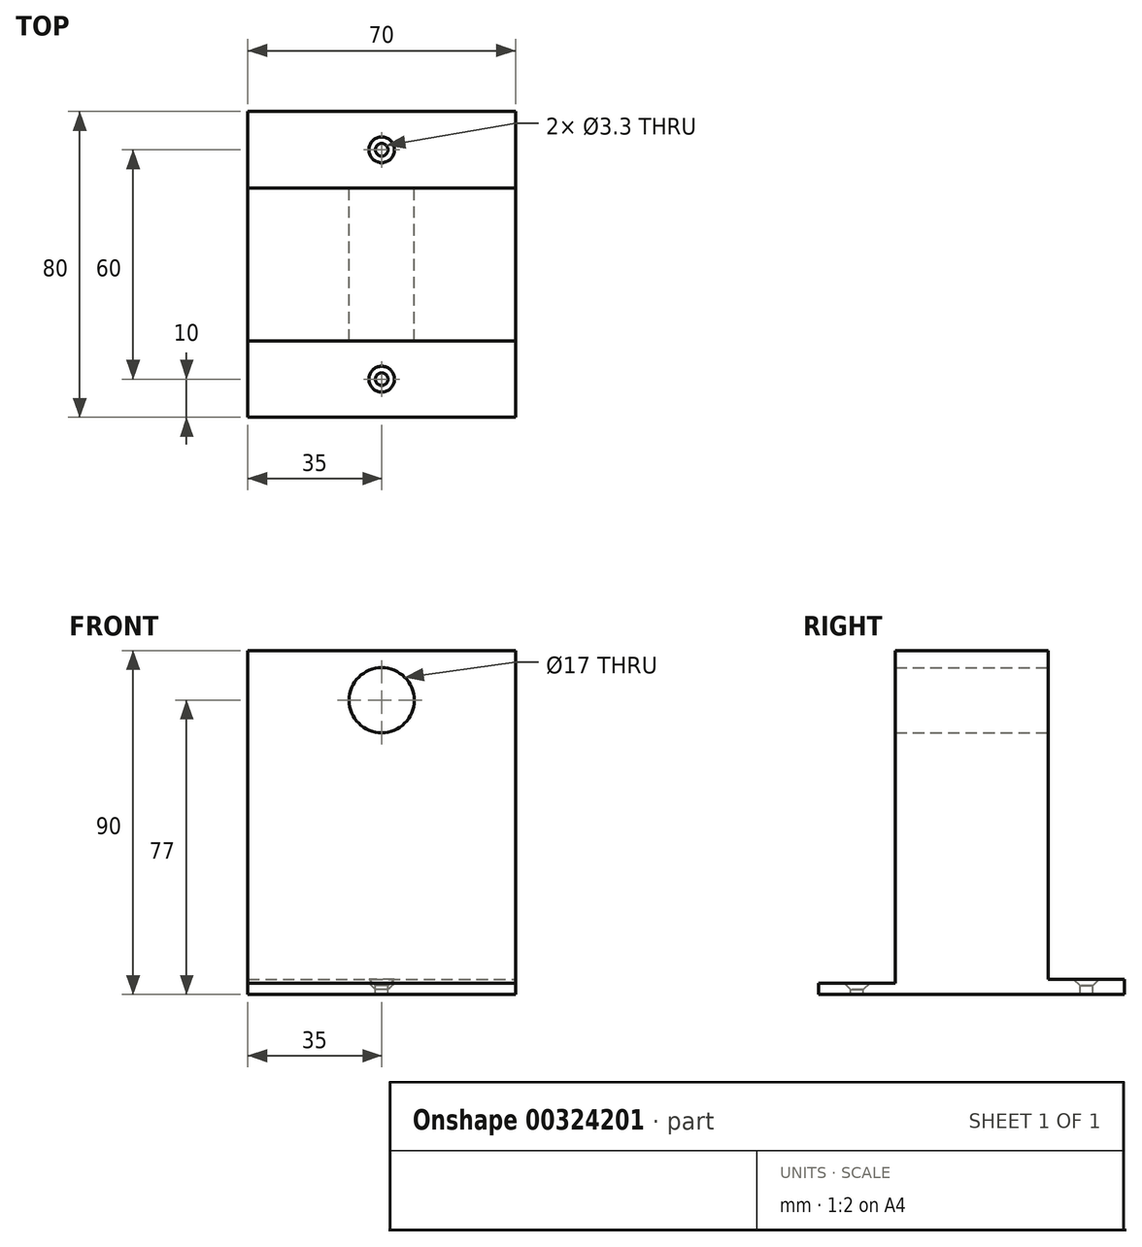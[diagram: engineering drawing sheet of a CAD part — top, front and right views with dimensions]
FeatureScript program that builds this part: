
annotation { "Feature Type Name" : "Feature", "Feature Type Description" : "" }
export const myFeature = defineFeature(function(context is Context, id is Id, definition is map)
    precondition{}
    {
        {
            var Q0;
            Q0=qCreatedBy(makeId("Top.planeOp"),FACE);
            var sketch = newSketch(context, id + "F0", { "sketchPlane" : qUnion([Q0])});
            skLineSegment(sketch, "E0.bottom", {"start": v(-35, 20) * mm, "end": v(35, 20) * mm});
            skLineSegment(sketch, "E0.top", {"start": v(-35, -20) * mm, "end": v(35, -20) * mm});
            skLineSegment(sketch, "E0.left", {"start": v(-35, 20) * mm, "end": v(-35, -20) * mm});
            skLineSegment(sketch, "E0.right", {"start": v(35, 20) * mm, "end": v(35, -20) * mm});
            skSolve(sketch);
        }
        {
            var Q0;
            Q0 = qSketchRegion(id + "F0", true);
            extrude(context, id + "F1", {"entities" : qUnion([Q0]), "depth" : 90 * mm});
        }
        {
            var Q0;
            Q0=makeQuery(id+"F1.opExtrude","SWEPT_FACE",FACE,{"disambiguationData":[OSD([sQuery(id+"F0.wireOp",EDGE,"E0.bottom")])]});
            var sketch = newSketch(context, id + "F2", { "sketchPlane" : qUnion([Q0])});
            skCircle(sketch, "E1", {"center": v(0, 77) * mm, "radius": 8.5 * mm});
            skLineSegment(sketch, "E2", {"start": v(0, 77) * mm, "end": v(0, 0) * mm});
            skSolve(sketch);
        }
        {
            var Q0;
            Q0 = qSketchRegion(id + "F2", true);
            extrude(context, id + "F3", {"entities" : qUnion([Q0]), "operationType" : NewBodyOperationType.REMOVE, "endBound" : BoundingType.THROUGH_ALL, "oppositeDirection" : true, "depth" : 25 * mm});
        }
        {
            var Q0;
            Q0=makeQuery(id+"F1.opExtrude","SWEPT_FACE",FACE,{"disambiguationData":[OSD([sQuery(id+"F0.wireOp",EDGE,"E0.top")])]});
            var sketch = newSketch(context, id + "F4", { "sketchPlane" : qUnion([Q0])});
            skLineSegment(sketch, "E3.bottom", {"start": v(-35, 3) * mm, "end": v(35, 3) * mm});
            skLineSegment(sketch, "E3.top", {"start": v(-35, 0) * mm, "end": v(35, 0) * mm});
            skLineSegment(sketch, "E3.left", {"start": v(-35, 3) * mm, "end": v(-35, 0) * mm});
            skLineSegment(sketch, "E3.right", {"start": v(35, 3) * mm, "end": v(35, 0) * mm});
            skSolve(sketch);
        }
        {
            var Q0;
            Q0 = qSketchRegion(id + "F4", true);
            extrude(context, id + "F5", {"entities" : qUnion([Q0]), "operationType" : NewBodyOperationType.ADD, "depth" : 20 * mm});
        }
        {
            var Q0;
            Q0=makeQuery(id+"F1.opExtrude","SWEPT_FACE",FACE,{"disambiguationData":[OSD([sQuery(id+"F0.wireOp",EDGE,"E0.bottom")])]});
            var sketch = newSketch(context, id + "F6", { "sketchPlane" : qUnion([Q0])});
            skLineSegment(sketch, "E4.bottom", {"start": v(35, 0) * mm, "end": v(-35, 0) * mm});
            skLineSegment(sketch, "E4.top", {"start": v(35, 4) * mm, "end": v(-35, 4) * mm});
            skLineSegment(sketch, "E4.left", {"start": v(35, 0) * mm, "end": v(35, 4) * mm});
            skLineSegment(sketch, "E4.right", {"start": v(-35, 0) * mm, "end": v(-35, 4) * mm});
            skSolve(sketch);
        }
        {
            var Q0;
            Q0 = qSketchRegion(id + "F6", true);
            extrude(context, id + "F7", {"entities" : qUnion([Q0]), "operationType" : NewBodyOperationType.ADD, "depth" : 20 * mm});
        }
        {
            var Q0;
            Q0=makeQuery(id+"F5.opExtrude","SWEPT_FACE",FACE,{"disambiguationData":[OSD([sQuery(id+"F4.wireOp",EDGE,"E3.bottom")])]});
            var sketch = newSketch(context, id + "F8", { "sketchPlane" : qUnion([Q0])});
            skLineSegment(sketch, "E5", {"start": v(-35, -20) * mm, "end": v(35, -40) * mm});
            skLineSegment(sketch, "E6", {"start": v(-35, -40) * mm, "end": v(35, -20) * mm});
            skPoint(sketch, "E7", {"position": v(0, -30) * mm});
            skSolve(sketch);
        }
        {
            var Q0;
            Q0=sQuery(id+"F8.wireOp",VERTEX,"E7");
            var Q1;
            Q1=makeQuery(id+"F1.opExtrude","SWEPT_BODY",BODY,{"disambiguationData":[OSD([sQuery(id+"F0.wireOp",EDGE,"E0.bottom"),sQuery(id+"F0.wireOp",EDGE,"E0.top"),sQuery(id+"F0.wireOp",EDGE,"E0.left"),sQuery(id+"F0.wireOp",EDGE,"E0.right")])]});
            hole(context, id + "F9", {"style" : HoleStyle.C_SINK, "endStyle" : HoleEndStyle.BLIND, "standardTappedOrClearance" : lookupTablePath({ "standard" : "ISO", "fit" : "Normal", "size" : "M3", "type" : "Clearance" }), "standardBlindInLast" : lookupTablePath({ "fit" : "Standard", "standard" : "ISO", "size" : "M3", "type" : "Clearance" }), "holeDiameter" : 3.3 * mm, "cSinkDiameter" : 6.72 * mm, "cSinkAngle" : 90 * degree, "holeDepth" : 12 * mm, "tappedDepth" : 12 * mm, "tapClearance" : 3, "startFromSketch" : true, "locations" : qUnion([Q0]), "scope" : qUnion([Q1])});
        }
        {
            var Q0;
            Q0=makeQuery(id+"F7.opExtrude","SWEPT_FACE",FACE,{"disambiguationData":[OSD([sQuery(id+"F6.wireOp",EDGE,"E4.top")])]});
            var sketch = newSketch(context, id + "F10", { "sketchPlane" : qUnion([Q0])});
            skLineSegment(sketch, "E8", {"start": v(-35, 40) * mm, "end": v(35, 20) * mm});
            skLineSegment(sketch, "E9", {"start": v(35, 20) * mm, "end": v(35, 40) * mm});
            skLineSegment(sketch, "E10", {"start": v(35, 40) * mm, "end": v(-35, 20) * mm});
            skPoint(sketch, "E11", {"position": v(0, 30) * mm});
            skSolve(sketch);
        }
        {
            var Q0;
            Q0=sQuery(id+"F10.wireOp",VERTEX,"E11");
            var Q1;
            Q1=makeQuery(id+"F1.opExtrude","SWEPT_BODY",BODY,{"disambiguationData":[OSD([sQuery(id+"F0.wireOp",EDGE,"E0.bottom"),sQuery(id+"F0.wireOp",EDGE,"E0.top"),sQuery(id+"F0.wireOp",EDGE,"E0.left"),sQuery(id+"F0.wireOp",EDGE,"E0.right")])]});
            hole(context, id + "F11", {"style" : HoleStyle.C_SINK, "endStyle" : HoleEndStyle.BLIND, "standardTappedOrClearance" : lookupTablePath({ "standard" : "ISO", "fit" : "Normal", "size" : "M3", "type" : "Clearance" }), "standardBlindInLast" : lookupTablePath({ "fit" : "Standard", "standard" : "ISO", "size" : "M3", "type" : "Clearance" }), "holeDiameter" : 3.3 * mm, "cSinkDiameter" : 6.72 * mm, "cSinkAngle" : 90 * degree, "holeDepth" : 12 * mm, "tappedDepth" : 12 * mm, "tapClearance" : 3, "startFromSketch" : true, "locations" : qUnion([Q0]), "scope" : qUnion([Q1])});
        }
    });
